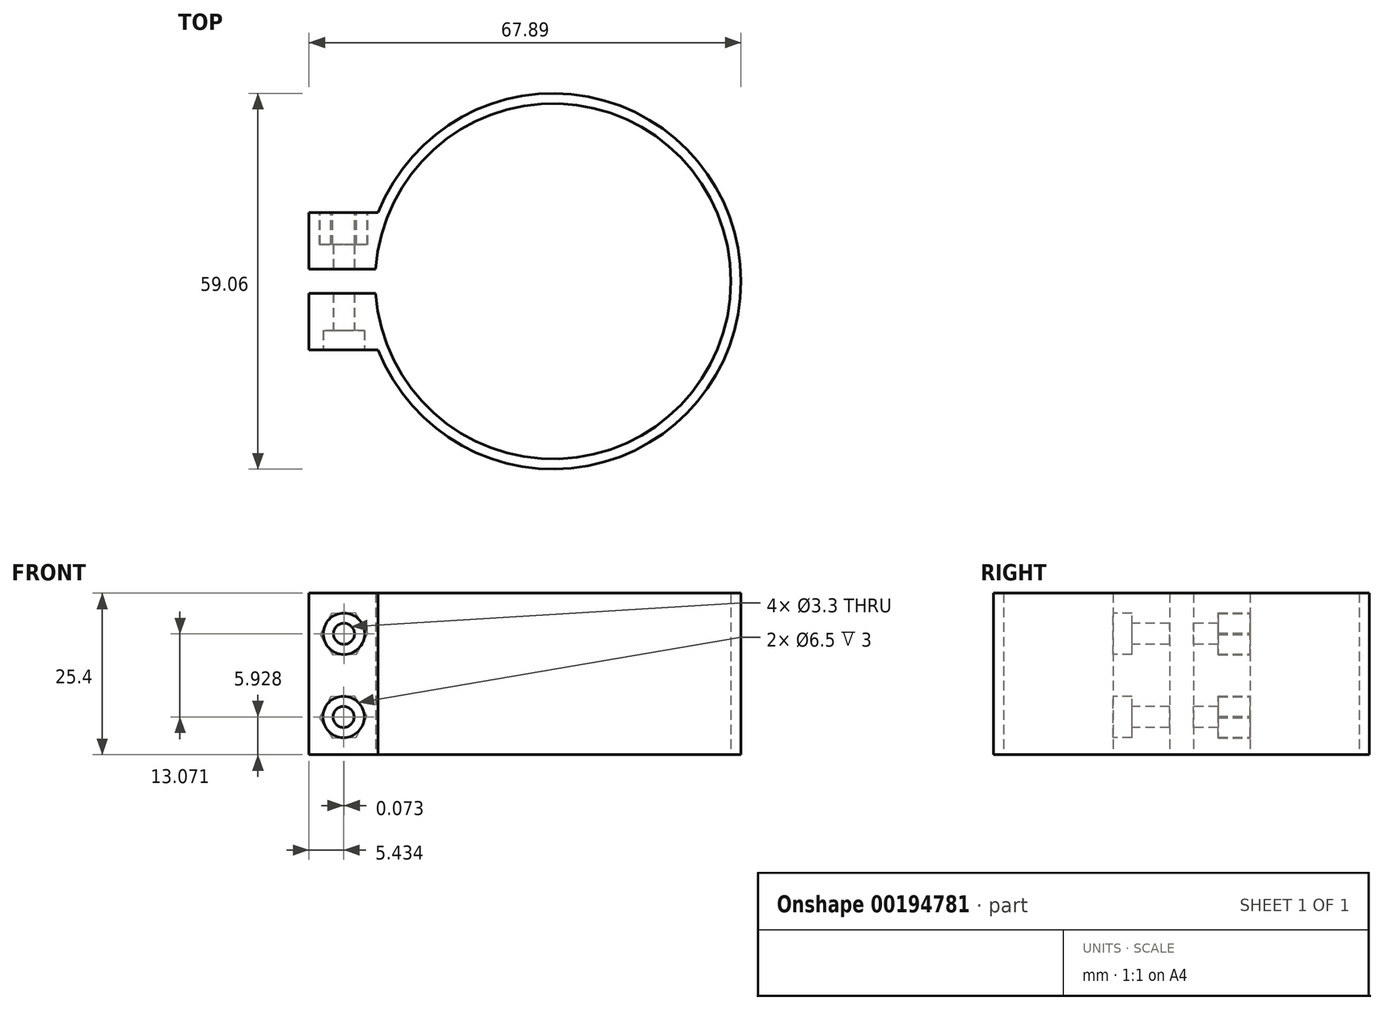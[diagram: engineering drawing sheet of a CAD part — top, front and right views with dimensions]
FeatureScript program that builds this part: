
annotation { "Feature Type Name" : "Feature", "Feature Type Description" : "" }
export const myFeature = defineFeature(function(context is Context, id is Id, definition is map)
    precondition{}
    {
        {
            var Q0;
            Q0=qCreatedBy(makeId("Top.planeOp"),FACE);
            var sketch = newSketch(context, id + "F0", { "sketchPlane" : qUnion([Q0])});
            skArc(sketch, "E0", {"start": v(-27.88, -1.88) * mm, "mid": v(27.94, 0) * mm, "end": v(-27.88, 1.88) * mm});
            skArc(sketch, "E1.0", {"start": v(-27.5, -10.77) * mm, "mid": v(29.53, 0) * mm, "end": v(-27.5, 10.77) * mm});
            skLineSegment(sketch, "E2.bottom", {"start": v(-27.88, -1.88) * mm, "end": v(-29.47, -1.88) * mm});
            skLineSegment(sketch, "E2.top", {"start": v(-27.88, 1.88) * mm, "end": v(-29.47, 1.88) * mm});
            skLineSegment(sketch, "E3.bottom", {"start": v(-29.47, 1.88) * mm, "end": v(-38.36, 1.88) * mm});
            skLineSegment(sketch, "E3.top", {"start": v(-29.47, 10.77) * mm, "end": v(-38.36, 10.77) * mm});
            skLineSegment(sketch, "E3.right", {"start": v(-38.36, 1.88) * mm, "end": v(-38.36, 10.77) * mm});
            skLineSegment(sketch, "E4.bottom", {"start": v(-29.47, -1.88) * mm, "end": v(-38.36, -1.88) * mm});
            skLineSegment(sketch, "E4.top", {"start": v(-29.47, -10.77) * mm, "end": v(-38.36, -10.77) * mm});
            skLineSegment(sketch, "E4.right", {"start": v(-38.36, -1.88) * mm, "end": v(-38.36, -10.77) * mm});
            skLineSegment(sketch, "E5", {"start": v(-29.47, 10.77) * mm, "end": v(-27.5, 10.77) * mm});
            skLineSegment(sketch, "E6", {"start": v(-29.47, -10.77) * mm, "end": v(-27.5, -10.77) * mm});
            skSolve(sketch);
        }
        {
            var Q0;
            Q0=makeQuery(id+"F0.imprint","IMPRINT",FACE,{"disambiguationData":[TD([[makeQuery(id+"F0.imprint","IMPRINT",EDGE,{"derivedFrom":sQuery(id+"F0.wireOp",EDGE,"E0")}),-1.0]])]});
            extrude(context, id + "F1", {"entities" : qUnion([Q0]), "depth" : 25.4 * mm});
        }
        {
            var Q0;
            Q0=makeQuery(id+"F1.opExtrude","SWEPT_FACE",FACE,{"disambiguationData":[OSD([sQuery(id+"F0.wireOp",EDGE,"E4.top"),sQuery(id+"F0.wireOp",EDGE,"E6")])]});
            var sketch = newSketch(context, id + "F2", { "sketchPlane" : qUnion([Q0])});
            skLineSegment(sketch, "E7", {"start": v(-32.93, 25.4) * mm, "end": v(-32.93, 0) * mm});
            skPoint(sketch, "E8", {"position": v(-32.85, 19) * mm});
            skPoint(sketch, "E9", {"position": v(-32.93, 5.93) * mm});
            skSolve(sketch);
        }
        {
            var Q0;
            Q0=sQuery(id+"F2.wireOp",VERTEX,"E8");
            var Q1;
            Q1=sQuery(id+"F2.wireOp",VERTEX,"E9");
            var Q2;
            Q2=makeQuery(id+"F1.opExtrude","SWEPT_BODY",BODY,{"disambiguationData":[OSD([sQuery(id+"F0.wireOp",EDGE,"E0"),sQuery(id+"F0.wireOp",EDGE,"E1.0"),sQuery(id+"F0.wireOp",EDGE,"E2.bottom"),sQuery(id+"F0.wireOp",EDGE,"E2.top"),sQuery(id+"F0.wireOp",EDGE,"E3.bottom"),sQuery(id+"F0.wireOp",EDGE,"E3.top"),sQuery(id+"F0.wireOp",EDGE,"E3.right"),sQuery(id+"F0.wireOp",EDGE,"E4.bottom"),sQuery(id+"F0.wireOp",EDGE,"E4.top"),sQuery(id+"F0.wireOp",EDGE,"E4.right"),sQuery(id+"F0.wireOp",EDGE,"E5"),sQuery(id+"F0.wireOp",EDGE,"E6")])]});
            hole(context, id + "F3", {"style" : HoleStyle.C_BORE, "endStyle" : HoleEndStyle.THROUGH, "standardTappedOrClearance" : lookupTablePath({ "standard" : "ISO", "fit" : "Normal", "size" : "M3", "type" : "Clearance" }), "standardBlindInLast" : lookupTablePath({ "fit" : "Standard", "standard" : "ISO", "size" : "M3", "type" : "Clearance" }), "holeDiameter" : 3.3 * mm, "cBoreDiameter" : 6.5 * mm, "cBoreDepth" : 3 * mm, "locations" : qUnion([Q0, Q1]), "scope" : qUnion([Q2]), "isTappedThrough" : true});
        }
        {
            var Q0;
            Q0=makeQuery(id+"F1.opExtrude","SWEPT_FACE",FACE,{"disambiguationData":[OSD([sQuery(id+"F0.wireOp",EDGE,"E3.top"),sQuery(id+"F0.wireOp",EDGE,"E5")])]});
            var sketch = newSketch(context, id + "F4", { "sketchPlane" : qUnion([Q0])});
            skCircle(sketch, "E10.cCircle", {"center": v(32.85, 19) * mm, "radius": 3.25 * mm, "construction": true});
            skLineSegment(sketch, "E10.0", {"start": v(36.6, 18.86) * mm, "end": v(34.6, 15.69) * mm});
            skLineSegment(sketch, "E10.1", {"start": v(34.6, 15.69) * mm, "end": v(30.86, 15.82) * mm});
            skLineSegment(sketch, "E10.2", {"start": v(30.86, 15.82) * mm, "end": v(29.1, 19.13) * mm});
            skLineSegment(sketch, "E10.3", {"start": v(29.1, 19.13) * mm, "end": v(31.1, 22.31) * mm});
            skLineSegment(sketch, "E10.4", {"start": v(31.1, 22.31) * mm, "end": v(34.84, 22.18) * mm});
            skLineSegment(sketch, "E10.5", {"start": v(34.84, 22.18) * mm, "end": v(36.6, 18.86) * mm});
            skPoint(sketch, "E10.0.midPoint", {"position": v(35.6, 17.27) * mm});
            skLineSegment(sketch, "E11.1.0.0", {"start": v(34.94, 9.1) * mm, "end": v(36.7, 5.78) * mm});
            skLineSegment(sketch, "E11.1.0.1", {"start": v(31.2, 9.23) * mm, "end": v(34.94, 9.1) * mm});
            skLineSegment(sketch, "E11.1.0.2", {"start": v(29.2, 6.06) * mm, "end": v(31.2, 9.23) * mm});
            skLineSegment(sketch, "E11.1.0.3", {"start": v(30.96, 2.74) * mm, "end": v(29.2, 6.06) * mm});
            skLineSegment(sketch, "E11.1.0.4", {"start": v(34.7, 2.6) * mm, "end": v(30.96, 2.74) * mm});
            skPoint(sketch, "E11.1.0.5", {"position": v(35.7, 4.2) * mm});
            skCircle(sketch, "E11.1.0.6", {"center": v(32.95, 5.92) * mm, "radius": 3.25 * mm, "construction": true});
            skLineSegment(sketch, "E11.1.0.7", {"start": v(36.7, 5.78) * mm, "end": v(34.7, 2.6) * mm});
            skLineSegment(sketch, "E11.direction1", {"start": v(30.86, 15.82) * mm, "end": v(30.96, 2.74) * mm, "construction": true});
            skSolve(sketch);
        }
        {
            var Q0;
            Q0=qSketchRegion(id+"F4",true);
            extrude(context, id + "F5", {"entities" : qUnion([Q0]), "operationType" : NewBodyOperationType.REMOVE, "oppositeDirection" : true, "depth" : 5 * mm});
        }
    });
